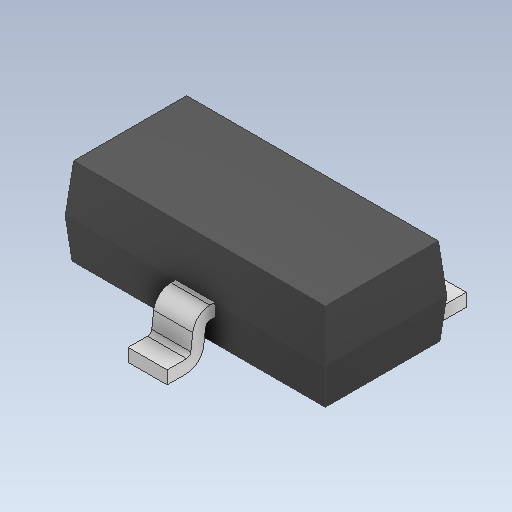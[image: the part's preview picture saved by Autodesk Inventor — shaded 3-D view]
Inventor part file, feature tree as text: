
AUTODESK INVENTOR PART (.ipt)
format: ipt  version: 2020 (Build 240168000, 168)  size: 127,488 bytes
history: native  units: mm
features: other x1, fillet x1
ambient origin geometry x8: Origin, YZ Plane, XZ Plane, XY Plane, X Axis, Y Axis, Z Axis, Center Point
bodies: Body1 (feature_tree)
feature tree (2):
  other  "Твердое тело1"
  fillet  "Fillet2"  [1 undecoded]
note: 1 required parameter value undecoded (feature->parameter linkage not recoverable at this tier; creation-order binding heuristic only, values carry confidence <= 0.55)
